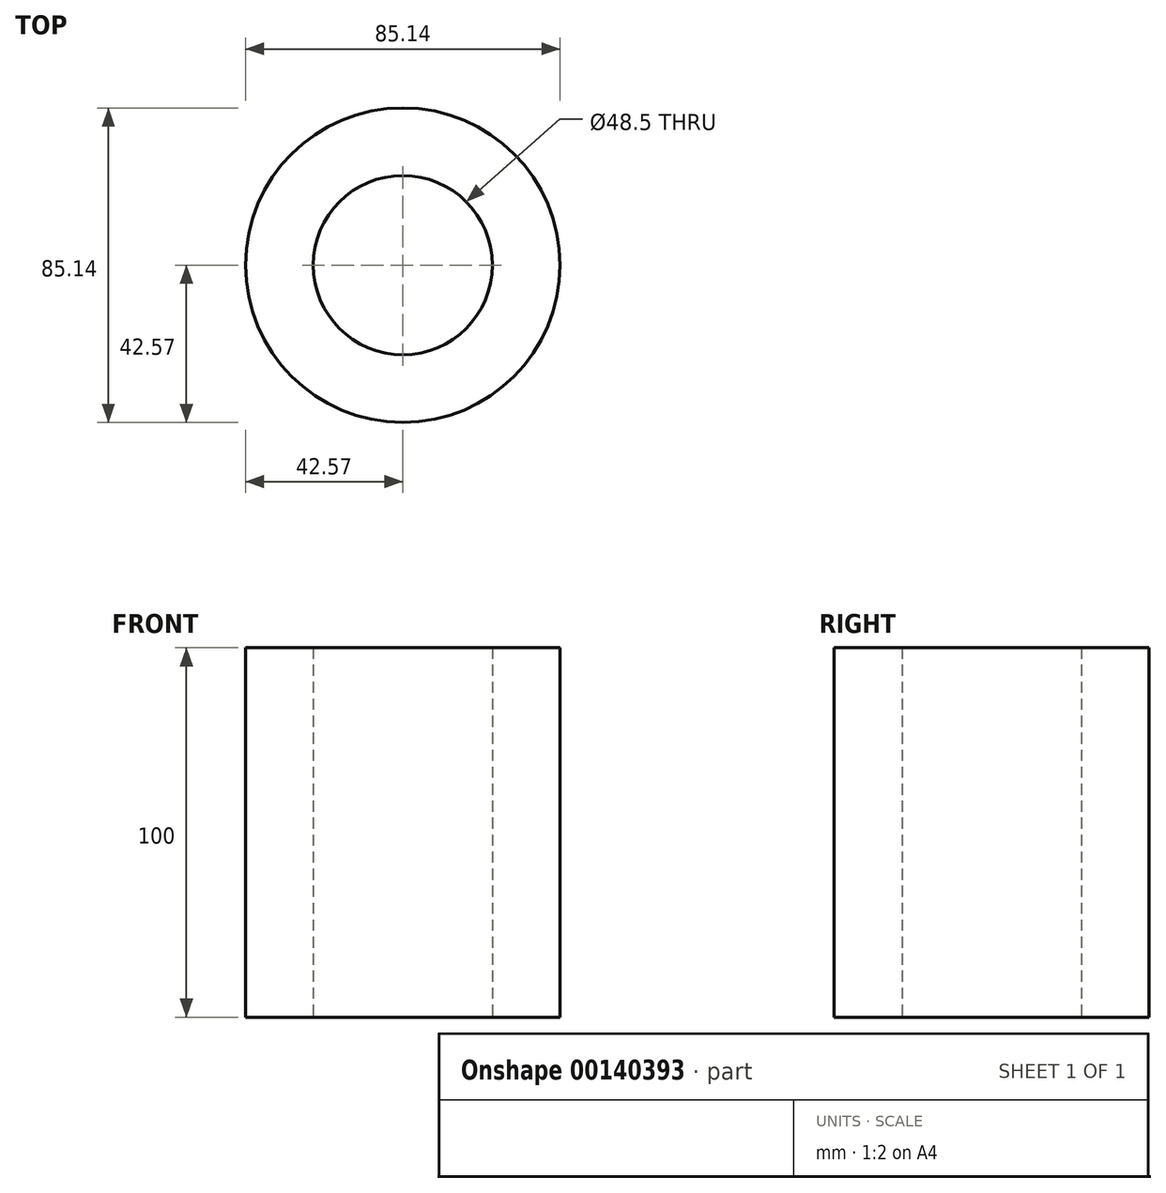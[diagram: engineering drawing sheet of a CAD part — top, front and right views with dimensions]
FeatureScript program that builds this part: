
annotation { "Feature Type Name" : "Feature", "Feature Type Description" : "" }
export const myFeature = defineFeature(function(context is Context, id is Id, definition is map)
    precondition{}
    {
        {
            var Q0;
            Q0=qCreatedBy(makeId("Top.planeOp"),FACE);
            var sketch = newSketch(context, id + "F0", { "sketchPlane" : qUnion([Q0])});
            skCircle(sketch, "E0", {"center": v(0, 0) * mm, "radius": 24.25 * mm});
            skCircle(sketch, "E1", {"center": v(0, 0) * mm, "radius": 42.57 * mm});
            skSolve(sketch);
        }
        {
            var Q0;
            Q0 = qSketchRegion(id + "F0", true);
            extrude(context, id + "F1", {"entities" : qUnion([Q0]), "depth" : 100 * mm});
        }
    });
